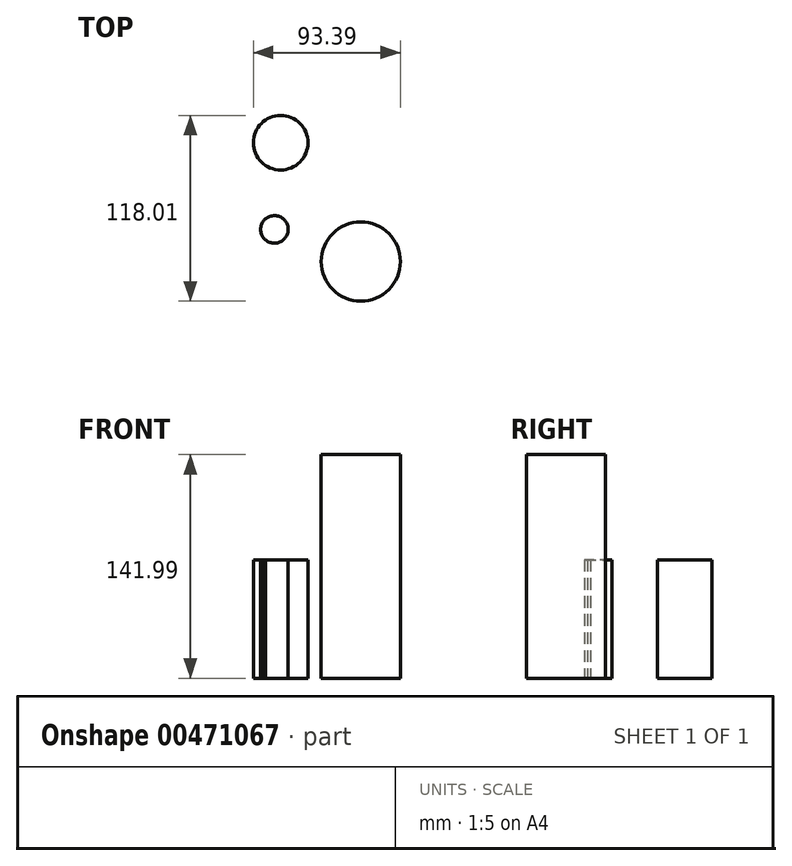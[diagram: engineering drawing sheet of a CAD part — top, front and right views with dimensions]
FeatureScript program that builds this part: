
annotation { "Feature Type Name" : "Feature", "Feature Type Description" : "" }
export const myFeature = defineFeature(function(context is Context, id is Id, definition is map)
    precondition{}
    {
        {
            var Q0;
            Q0=qCreatedBy(makeId("Top.planeOp"),FACE);
            var sketch = newSketch(context, id + "F0", { "sketchPlane" : qUnion([Q0])});
            skCircle(sketch, "E0", {"center": v(-80.1, -53.2) * mm, "radius": 25.14 * mm});
            skCircle(sketch, "E1", {"center": v(-131, 22.33) * mm, "radius": 17.36 * mm});
            skCircle(sketch, "E2", {"center": v(-134.96, -32.76) * mm, "radius": 8.74 * mm});
            skCircle(sketch, "E3", {"center": v(-138.8, -36.04) * mm, "radius": 3.82 * mm});
            skSolve(sketch);
        }
        {
            var Q0;
            Q0 = qSketchRegion(id + "F0", true);
            extrude(context, id + "F1", {"entities" : qUnion([Q0]), "depth" : 75.18 * mm});
        }
        {
            var Q0;
            Q0=makeQuery(id+"F1.opExtrude","CAP_FACE",FACE,{"disambiguationData":[OSD([sQuery(id+"F0.wireOp",EDGE,"E0")])],"isStart":false});
            extrude(context, id + "F2", {"entities" : qUnion([Q0]), "operationType" : NewBodyOperationType.ADD, "depth" : 66.8 * mm});
        }
    });
